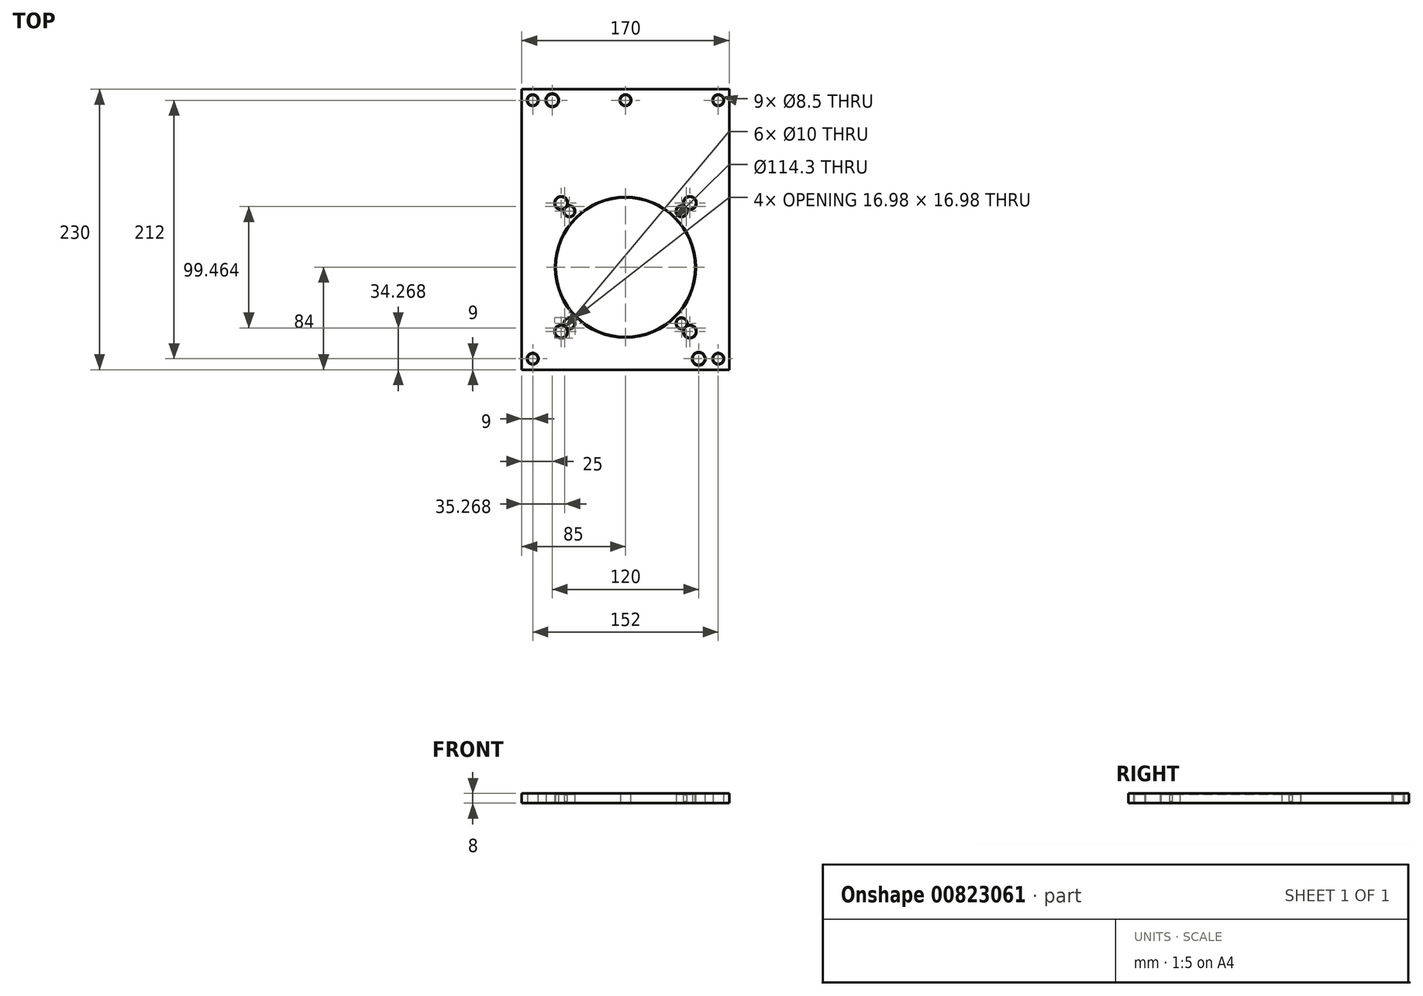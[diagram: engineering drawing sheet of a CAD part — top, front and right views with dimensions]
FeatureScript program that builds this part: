
annotation { "Feature Type Name" : "Feature", "Feature Type Description" : "" }
export const myFeature = defineFeature(function(context is Context, id is Id, definition is map)
    precondition{}
    {
        {
            var Q0;
            Q0=qCreatedBy(makeId("Top.planeOp"),FACE);
            var sketch = newSketch(context, id + "F0", { "sketchPlane" : qUnion([Q0])});
            skCircle(sketch, "E0", {"center": v(0, 0) * mm, "radius": 55 * mm});
            skLineSegment(sketch, "E1", {"start": v(0, 0) * mm, "end": v(152.93, 0) * mm, "construction": true});
            skLineSegment(sketch, "E2", {"start": v(0, 194.5) * mm, "end": v(0, 0) * mm, "construction": true});
            skCircle(sketch, "E3", {"center": v(0, 0) * mm, "radius": 65 * mm, "construction": true});
            skLineSegment(sketch, "E4", {"start": v(0, 0) * mm, "end": v(45.96, 45.96) * mm, "construction": true});
            skCircle(sketch, "E5", {"center": v(45.96, 45.96) * mm, "radius": 4.25 * mm});
            skCircle(sketch, "E6.1.0", {"center": v(-45.96, 45.96) * mm, "radius": 4.25 * mm});
            skCircle(sketch, "E6.2.0", {"center": v(-45.96, -45.96) * mm, "radius": 4.25 * mm});
            skCircle(sketch, "E6.3.0", {"center": v(45.96, -45.96) * mm, "radius": 4.25 * mm});
            skLineSegment(sketch, "E7.bottom", {"start": v(85, -84) * mm, "end": v(-85, -84) * mm});
            skLineSegment(sketch, "E7.top", {"start": v(85, 146) * mm, "end": v(-85, 146) * mm});
            skLineSegment(sketch, "E7.left", {"start": v(85, -84) * mm, "end": v(85, 146) * mm});
            skLineSegment(sketch, "E7.right", {"start": v(-85, -84) * mm, "end": v(-85, 146) * mm});
            skPoint(sketch, "E7.middle", {"position": v(0, 31) * mm});
            skCircle(sketch, "E8", {"center": v(0, 0) * mm, "radius": 80 * mm, "construction": true});
            skLineSegment(sketch, "E9.0", {"start": v(85, -66) * mm, "end": v(-85, -66) * mm, "construction": true});
            skLineSegment(sketch, "E10.0", {"start": v(85, 128) * mm, "end": v(-85, 128) * mm, "construction": true});
            skLineSegment(sketch, "E11", {"start": v(-85, 137) * mm, "end": v(85, 137) * mm, "construction": true});
            skLineSegment(sketch, "E12", {"start": v(-85, -75) * mm, "end": v(85, -75) * mm, "construction": true});
            skLineSegment(sketch, "E13.0", {"start": v(-76, -84) * mm, "end": v(-76, 146) * mm, "construction": true});
            skLineSegment(sketch, "E14.0", {"start": v(76, -84) * mm, "end": v(76, 146) * mm, "construction": true});
            skCircle(sketch, "E15", {"center": v(-76, 137) * mm, "radius": 4.25 * mm});
            skCircle(sketch, "E16", {"center": v(76, 137) * mm, "radius": 4.25 * mm});
            skCircle(sketch, "E17", {"center": v(76, -75) * mm, "radius": 4.25 * mm});
            skCircle(sketch, "E18", {"center": v(-76, -75) * mm, "radius": 4.25 * mm});
            skCircle(sketch, "E19", {"center": v(60, -75) * mm, "radius": 5 * mm});
            skCircle(sketch, "E20", {"center": v(-60, 137) * mm, "radius": 5 * mm});
            skCircle(sketch, "E21", {"center": v(0, 137) * mm, "radius": 4.25 * mm});
            skSolve(sketch);
        }
        {
            var Q0;
            Q0=qSketchRegion(id+"F0",true);
            extrude(context, id + "F1", {"entities" : qUnion([Q0]), "depth" : 8 * mm, "offsetDistance" : 25 * mm});
        }
        {
            var Q0;
            Q0=makeQuery(id+"F1.opExtrude","SWEPT_FACE",FACE,{"disambiguationData":[OSD([sQuery(id+"F0.wireOp",EDGE,"E18")])]});
            var Q1;
            Q1=makeQuery(id+"F1.opExtrude","SWEPT_FACE",FACE,{"disambiguationData":[OSD([sQuery(id+"F0.wireOp",EDGE,"E6.2.0")])]});
            var Q2;
            Q2=makeQuery(id+"F1.opExtrude","SWEPT_FACE",FACE,{"disambiguationData":[OSD([sQuery(id+"F0.wireOp",EDGE,"E19")])]});
            var Q3;
            Q3=makeQuery(id+"F1.opExtrude","SWEPT_FACE",FACE,{"disambiguationData":[OSD([sQuery(id+"F0.wireOp",EDGE,"E6.3.0")])]});
            var Q4;
            Q4=makeQuery(id+"F1.opExtrude","SWEPT_FACE",FACE,{"disambiguationData":[OSD([sQuery(id+"F0.wireOp",EDGE,"E5")])]});
            var Q5;
            Q5=makeQuery(id+"F1.opExtrude","SWEPT_FACE",FACE,{"disambiguationData":[OSD([sQuery(id+"F0.wireOp",EDGE,"E6.1.0")])]});
            var Q6;
            Q6=makeQuery(id+"F1.opExtrude","SWEPT_FACE",FACE,{"disambiguationData":[OSD([sQuery(id+"F0.wireOp",EDGE,"E0")])]});
            var Q7;
            Q7=makeQuery(id+"F1.opExtrude","SWEPT_FACE",FACE,{"disambiguationData":[OSD([sQuery(id+"F0.wireOp",EDGE,"E17")])]});
            var Q8;
            Q8=makeQuery(id+"F1.opExtrude","SWEPT_FACE",FACE,{"disambiguationData":[OSD([sQuery(id+"F0.wireOp",EDGE,"E16")])]});
            var Q9;
            Q9=makeQuery(id+"F1.opExtrude","SWEPT_FACE",FACE,{"disambiguationData":[OSD([sQuery(id+"F0.wireOp",EDGE,"E20")])]});
            var Q10;
            Q10=makeQuery(id+"F1.opExtrude","SWEPT_FACE",FACE,{"disambiguationData":[OSD([sQuery(id+"F0.wireOp",EDGE,"E15")])]});
            var Q11;
            Q11=makeQuery(id+"F1.opExtrude","SWEPT_FACE",FACE,{"disambiguationData":[OSD([sQuery(id+"F0.wireOp",EDGE,"E21")])]});
            chamfer(context, id + "F2", {"entities" : qUnion([Q0, Q1, Q2, Q3, Q4, Q5, Q6, Q7, Q8, Q9, Q10, Q11]), "width" : 0.5 * mm, "tangentPropagation" : true});
        }
        {
            var Q0;
            Q0=makeQuery(id+"F1.opExtrude","CAP_FACE",FACE,{"disambiguationData":[OSD([sQuery(id+"F0.wireOp",EDGE,"E0"),sQuery(id+"F0.wireOp",EDGE,"E5"),sQuery(id+"F0.wireOp",EDGE,"E6.1.0"),sQuery(id+"F0.wireOp",EDGE,"E6.2.0"),sQuery(id+"F0.wireOp",EDGE,"E6.3.0"),sQuery(id+"F0.wireOp",EDGE,"E7.bottom"),sQuery(id+"F0.wireOp",EDGE,"E7.top"),sQuery(id+"F0.wireOp",EDGE,"E7.left"),sQuery(id+"F0.wireOp",EDGE,"E7.right"),sQuery(id+"F0.wireOp",EDGE,"E15"),sQuery(id+"F0.wireOp",EDGE,"E16"),sQuery(id+"F0.wireOp",EDGE,"E17"),sQuery(id+"F0.wireOp",EDGE,"E18"),sQuery(id+"F0.wireOp",EDGE,"E19"),sQuery(id+"F0.wireOp",EDGE,"E20"),sQuery(id+"F0.wireOp",EDGE,"E21")])],"isStart":false});
            var sketch = newSketch(context, id + "F3", { "sketchPlane" : qUnion([Q0])});
            skCircle(sketch, "E22", {"center": v(0, 0) * mm, "radius": 57.15 * mm});
            skCircle(sketch, "E23", {"center": v(0, 0) * mm, "radius": 74.6 * mm, "construction": true});
            skLineSegment(sketch, "E24", {"start": v(0, 0) * mm, "end": v(113.3, 0) * mm, "construction": true});
            skLineSegment(sketch, "E25", {"start": v(0, 0) * mm, "end": v(98.28, 98.28) * mm, "construction": true});
            skCircle(sketch, "E26", {"center": v(52.75, 52.75) * mm, "radius": 5 * mm});
            skCircle(sketch, "E27.1.0", {"center": v(-52.75, 52.75) * mm, "radius": 5 * mm});
            skCircle(sketch, "E27.2.0", {"center": v(-52.75, -52.75) * mm, "radius": 5 * mm});
            skCircle(sketch, "E27.3.0", {"center": v(52.75, -52.75) * mm, "radius": 5 * mm});
            skSolve(sketch);
        }
        {
            var Q0;
            Q0 = qSketchRegion(id + "F3", true);
            extrude(context, id + "F4", {"entities" : qUnion([Q0]), "operationType" : NewBodyOperationType.REMOVE, "oppositeDirection" : true, "depth" : 25 * mm, "offsetDistance" : 25 * mm});
        }
        {
            var Q0;
            Q0=makeQuery(id+"F4.boolean.opBoolean","COPY",FACE,{"derivedFrom":makeQuery(id+"F4.opExtrude","SWEPT_FACE",FACE,{"disambiguationData":[OSD([sQuery(id+"F3.wireOp",EDGE,"E27.2.0")])]})});
            var Q1;
            Q1=makeQuery(id+"F4.boolean.opBoolean","COPY",FACE,{"derivedFrom":makeQuery(id+"F4.opExtrude","SWEPT_FACE",FACE,{"disambiguationData":[OSD([sQuery(id+"F3.wireOp",EDGE,"E22")])]})});
            var Q2;
            Q2=makeQuery(id+"F4.boolean.opBoolean","COPY",FACE,{"derivedFrom":makeQuery(id+"F4.opExtrude","SWEPT_FACE",FACE,{"disambiguationData":[OSD([sQuery(id+"F3.wireOp",EDGE,"E27.3.0")])]})});
            var Q3;
            Q3=makeQuery(id+"F4.boolean.opBoolean","COPY",FACE,{"derivedFrom":makeQuery(id+"F4.opExtrude","SWEPT_FACE",FACE,{"disambiguationData":[OSD([sQuery(id+"F3.wireOp",EDGE,"E26")])]})});
            var Q4;
            Q4=makeQuery(id+"F4.boolean.opBoolean","COPY",FACE,{"derivedFrom":makeQuery(id+"F4.opExtrude","SWEPT_FACE",FACE,{"disambiguationData":[OSD([sQuery(id+"F3.wireOp",EDGE,"E27.1.0")])]})});
            chamfer(context, id + "F5", {"entities" : qUnion([Q0, Q1, Q2, Q3, Q4]), "width" : 0.5 * mm, "tangentPropagation" : true});
        }
    });
